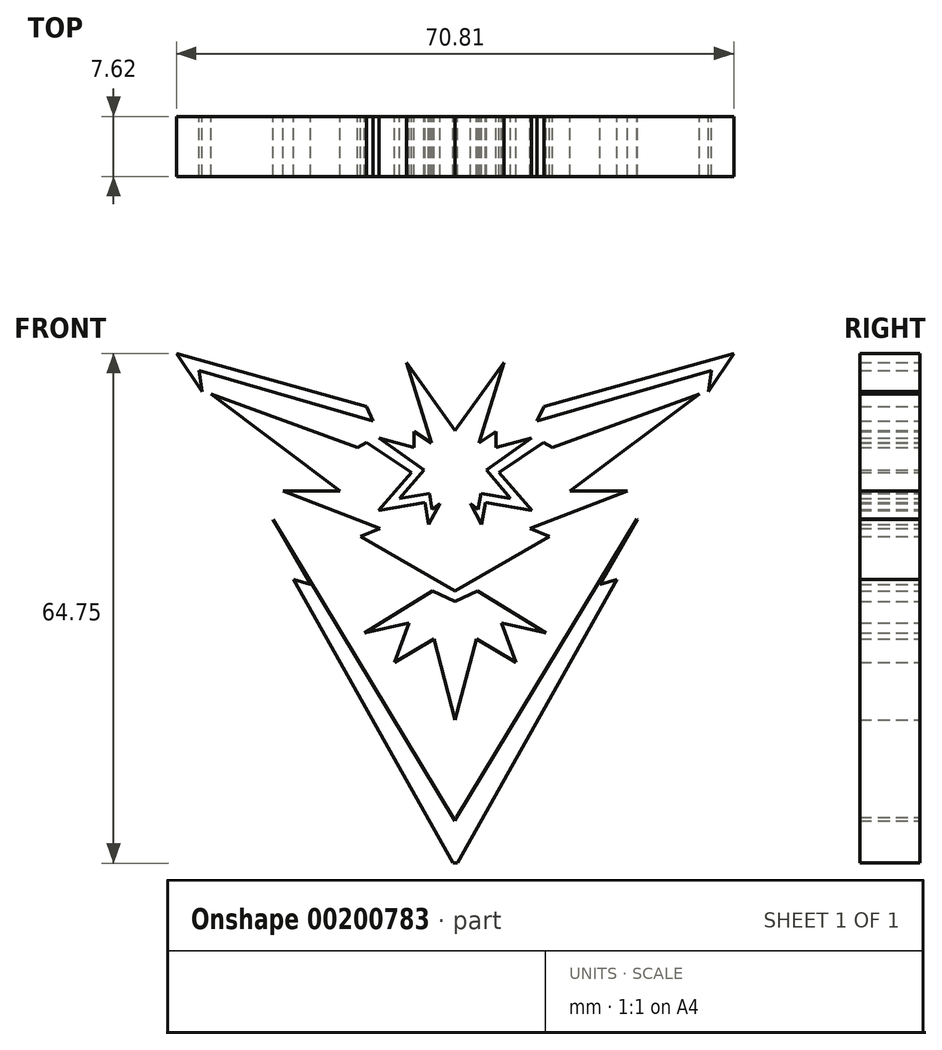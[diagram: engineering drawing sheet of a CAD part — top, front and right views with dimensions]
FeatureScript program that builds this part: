
annotation { "Feature Type Name" : "Feature", "Feature Type Description" : "" }
export const myFeature = defineFeature(function(context is Context, id is Id, definition is map)
    precondition{}
    {
        {
            var Q0;
            Q0=qCreatedBy(makeId("Front.planeOp"),FACE);
            var sketch = newSketch(context, id + "F0", { "sketchPlane" : qUnion([Q0])});
            skLineSegment(sketch, "E0", {"start": v(1.5, 35.4) * mm, "end": v(-4.67, 44.05) * mm});
            skLineSegment(sketch, "E1", {"start": v(-4.67, 44.05) * mm, "end": v(-1.5, 33.83) * mm});
            skLineSegment(sketch, "E2", {"start": v(-1.5, 33.83) * mm, "end": v(-3.69, 35.28) * mm});
            skLineSegment(sketch, "E3", {"start": v(-3.69, 35.28) * mm, "end": v(-3.69, 33.23) * mm});
            skLineSegment(sketch, "E4", {"start": v(-3.69, 33.23) * mm, "end": v(-8.18, 34.47) * mm});
            skLineSegment(sketch, "E5", {"start": v(-8.18, 34.47) * mm, "end": v(-2.45, 30.4) * mm});
            skLineSegment(sketch, "E6", {"start": v(-2.45, 30.4) * mm, "end": v(-5.53, 26.76) * mm});
            skLineSegment(sketch, "E7", {"start": v(-5.53, 26.76) * mm, "end": v(-1.76, 27.4) * mm});
            skLineSegment(sketch, "E8", {"start": v(-1.76, 27.4) * mm, "end": v(-1.42, 25.4) * mm});
            skLineSegment(sketch, "E9", {"start": v(-1.42, 25.4) * mm, "end": v(-0.44, 26.12) * mm});
            skLineSegment(sketch, "E10", {"start": v(-0.44, 26.12) * mm, "end": v(-1.85, 23.47) * mm});
            skLineSegment(sketch, "E11", {"start": v(-1.85, 23.47) * mm, "end": v(-2.32, 26.25) * mm});
            skLineSegment(sketch, "E12", {"start": v(-2.32, 26.25) * mm, "end": v(-8.22, 25.25) * mm});
            skLineSegment(sketch, "E13", {"start": v(-8.22, 25.25) * mm, "end": v(-4.03, 30.06) * mm});
            skLineSegment(sketch, "E14", {"start": v(-4.03, 30.06) * mm, "end": v(-9.72, 33.91) * mm});
            skLineSegment(sketch, "E15", {"start": v(-9.72, 33.91) * mm, "end": v(-10.88, 33.23) * mm});
            skLineSegment(sketch, "E16", {"start": v(-10.88, 33.23) * mm, "end": v(-29.5, 40.03) * mm});
            skLineSegment(sketch, "E17", {"start": v(-29.5, 40.03) * mm, "end": v(-13.1, 27.7) * mm});
            skLineSegment(sketch, "E18", {"start": v(-13.1, 27.7) * mm, "end": v(-20.38, 27.7) * mm});
            skLineSegment(sketch, "E19", {"start": v(-20.38, 27.7) * mm, "end": v(-8.01, 22.95) * mm});
            skLineSegment(sketch, "E20", {"start": v(-8.01, 22.95) * mm, "end": v(-10.5, 21.93) * mm});
            skLineSegment(sketch, "E21", {"start": v(-10.5, 21.93) * mm, "end": v(1.5, 15.01) * mm});
            skLineSegment(sketch, "E22", {"start": v(-1.35, 15.06) * mm, "end": v(-10.01, 9.67) * mm});
            skLineSegment(sketch, "E23", {"start": v(-10.01, 9.67) * mm, "end": v(-4.38, 10.97) * mm});
            skLineSegment(sketch, "E24", {"start": v(-4.38, 10.97) * mm, "end": v(-6.2, 5.95) * mm});
            skLineSegment(sketch, "E25", {"start": v(-6.2, 5.95) * mm, "end": v(-1.17, 8.91) * mm});
            skLineSegment(sketch, "E26", {"start": v(-1.17, 8.91) * mm, "end": v(1.5, -1.33) * mm});
            skLineSegment(sketch, "E27", {"start": v(-1.35, 15.06) * mm, "end": v(1.5, 13.7) * mm});
            skLineSegment(sketch, "E28", {"start": v(-33.9, 45.2) * mm, "end": v(-30.64, 40.35) * mm});
            skLineSegment(sketch, "E29", {"start": v(-30.64, 40.35) * mm, "end": v(-31.05, 43.05) * mm});
            skLineSegment(sketch, "E30", {"start": v(-31.05, 43.05) * mm, "end": v(-8.9, 36.6) * mm});
            skLineSegment(sketch, "E31", {"start": v(-8.9, 36.6) * mm, "end": v(-9.75, 38.47) * mm});
            skLineSegment(sketch, "E32", {"start": v(-9.75, 38.47) * mm, "end": v(-33.9, 45.2) * mm});
            skLineSegment(sketch, "E33", {"start": v(-21.64, 24.13) * mm, "end": v(-16.86, 15.86) * mm});
            skLineSegment(sketch, "E34", {"start": v(-16.86, 15.86) * mm, "end": v(-19.05, 16.5) * mm});
            skLineSegment(sketch, "E35", {"start": v(-19.05, 16.5) * mm, "end": v(1.24, -19.55) * mm});
            skLineSegment(sketch, "E36", {"start": v(-21.64, 24.13) * mm, "end": v(1.24, -13.77) * mm});
            skLineSegment(sketch, "E37.MirrorCS", {"start": v(22.07, 16.5) * mm, "end": v(1.78, -19.55) * mm});
            skLineSegment(sketch, "E38.MirrorCS", {"start": v(24.59, 24.18) * mm, "end": v(1.7, -13.72) * mm});
            skLineSegment(sketch, "E39.MirrorCS", {"start": v(19.88, 15.86) * mm, "end": v(22.07, 16.5) * mm});
            skLineSegment(sketch, "E40.MirrorCS", {"start": v(24.66, 24.13) * mm, "end": v(19.88, 15.86) * mm});
            skLineSegment(sketch, "E41.MirrorCS", {"start": v(4.37, 15.06) * mm, "end": v(13.02, 9.67) * mm});
            skLineSegment(sketch, "E42.MirrorCS", {"start": v(13.02, 9.67) * mm, "end": v(7.4, 10.97) * mm});
            skLineSegment(sketch, "E43.MirrorCS", {"start": v(9.21, 5.95) * mm, "end": v(4.19, 8.91) * mm});
            skLineSegment(sketch, "E44.MirrorCS", {"start": v(7.4, 10.97) * mm, "end": v(9.21, 5.95) * mm});
            skLineSegment(sketch, "E45.MirrorCS", {"start": v(4.19, 8.91) * mm, "end": v(1.5, -1.33) * mm});
            skLineSegment(sketch, "E46.MirrorCS", {"start": v(4.37, 15.06) * mm, "end": v(1.5, 13.7) * mm});
            skLineSegment(sketch, "E47.MirrorCS", {"start": v(13.5, 21.93) * mm, "end": v(1.5, 15.01) * mm});
            skLineSegment(sketch, "E48.MirrorCS", {"start": v(11.03, 22.95) * mm, "end": v(13.5, 21.93) * mm});
            skLineSegment(sketch, "E49.MirrorCS", {"start": v(23.4, 27.7) * mm, "end": v(11.03, 22.95) * mm});
            skLineSegment(sketch, "E50.MirrorCS", {"start": v(16.12, 27.7) * mm, "end": v(23.4, 27.7) * mm});
            skLineSegment(sketch, "E51.MirrorCS", {"start": v(32.51, 40.03) * mm, "end": v(16.12, 27.7) * mm});
            skLineSegment(sketch, "E52.MirrorCS", {"start": v(13.9, 33.23) * mm, "end": v(32.51, 40.03) * mm});
            skLineSegment(sketch, "E53.MirrorCS", {"start": v(12.74, 33.91) * mm, "end": v(13.9, 33.23) * mm});
            skLineSegment(sketch, "E54.MirrorCS", {"start": v(7.05, 30.06) * mm, "end": v(12.74, 33.91) * mm});
            skLineSegment(sketch, "E55.MirrorCS", {"start": v(11.24, 25.25) * mm, "end": v(7.05, 30.06) * mm});
            skLineSegment(sketch, "E56.MirrorCS", {"start": v(5.33, 26.25) * mm, "end": v(11.24, 25.25) * mm});
            skLineSegment(sketch, "E57.MirrorCS", {"start": v(4.86, 23.47) * mm, "end": v(5.33, 26.25) * mm});
            skLineSegment(sketch, "E58.MirrorCS", {"start": v(3.45, 26.12) * mm, "end": v(4.86, 23.47) * mm});
            skLineSegment(sketch, "E59.MirrorCS", {"start": v(4.44, 25.4) * mm, "end": v(3.45, 26.12) * mm});
            skLineSegment(sketch, "E60.MirrorCS", {"start": v(4.78, 27.4) * mm, "end": v(4.44, 25.4) * mm});
            skLineSegment(sketch, "E61.MirrorCS", {"start": v(8.54, 26.76) * mm, "end": v(4.78, 27.4) * mm});
            skLineSegment(sketch, "E62.MirrorCS", {"start": v(5.46, 30.4) * mm, "end": v(8.54, 26.76) * mm});
            skLineSegment(sketch, "E63.MirrorCS", {"start": v(11.2, 34.47) * mm, "end": v(5.46, 30.4) * mm});
            skLineSegment(sketch, "E64.MirrorCS", {"start": v(6.7, 33.23) * mm, "end": v(11.2, 34.47) * mm});
            skLineSegment(sketch, "E65.MirrorCS", {"start": v(6.7, 35.28) * mm, "end": v(6.7, 33.23) * mm});
            skLineSegment(sketch, "E66.MirrorCS", {"start": v(4.52, 33.83) * mm, "end": v(6.7, 35.28) * mm});
            skLineSegment(sketch, "E67.MirrorCS", {"start": v(7.69, 44.05) * mm, "end": v(4.52, 33.83) * mm});
            skLineSegment(sketch, "E68.MirrorCS", {"start": v(1.5, 35.4) * mm, "end": v(7.69, 44.05) * mm});
            skLineSegment(sketch, "E69.MirrorCS", {"start": v(34.06, 43.05) * mm, "end": v(11.91, 36.6) * mm});
            skLineSegment(sketch, "E70.MirrorCS", {"start": v(12.76, 38.47) * mm, "end": v(36.91, 45.2) * mm});
            skLineSegment(sketch, "E71.MirrorCS", {"start": v(11.91, 36.6) * mm, "end": v(12.76, 38.47) * mm});
            skLineSegment(sketch, "E72.MirrorCS", {"start": v(33.65, 40.35) * mm, "end": v(34.06, 43.05) * mm});
            skLineSegment(sketch, "E73.MirrorCS", {"start": v(36.91, 45.2) * mm, "end": v(33.65, 40.35) * mm});
            skLineSegment(sketch, "E74", {"start": v(1.24, -13.77) * mm, "end": v(1.47, -14.16) * mm});
            skLineSegment(sketch, "E75", {"start": v(1.47, -14.16) * mm, "end": v(1.7, -13.72) * mm});
            skLineSegment(sketch, "E76", {"start": v(1.24, -19.55) * mm, "end": v(1.78, -19.55) * mm});
            skLineSegment(sketch, "E77", {"start": v(24.59, 24.18) * mm, "end": v(24.66, 24.13) * mm});
            skSolve(sketch);
        }
        {
            var Q0;
            Q0=makeQuery(id+"F0.imprint","IMPRINT",FACE,{"disambiguationData":[TD([[makeQuery(id+"F0.imprint","IMPRINT",EDGE,{"derivedFrom":sQuery(id+"F0.wireOp",EDGE,"E69.MirrorCS")}),-1.0]])]});
            var Q1;
            Q1=makeQuery(id+"F0.imprint","IMPRINT",FACE,{"disambiguationData":[TD([[makeQuery(id+"F0.imprint","IMPRINT",EDGE,{"derivedFrom":sQuery(id+"F0.wireOp",EDGE,"E33")}),1.0]])]});
            var Q2;
            Q2=makeQuery(id+"F0.imprint","IMPRINT",FACE,{"disambiguationData":[TD([[makeQuery(id+"F0.imprint","IMPRINT",EDGE,{"derivedFrom":sQuery(id+"F0.wireOp",EDGE,"E22")}),1.0]])]});
            var Q3;
            Q3=makeQuery(id+"F0.imprint","IMPRINT",FACE,{"disambiguationData":[TD([[makeQuery(id+"F0.imprint","IMPRINT",EDGE,{"derivedFrom":sQuery(id+"F0.wireOp",EDGE,"E28")}),1.0]])]});
            var Q4;
            Q4=makeQuery(id+"F0.imprint","IMPRINT",FACE,{"disambiguationData":[TD([[makeQuery(id+"F0.imprint","IMPRINT",EDGE,{"derivedFrom":sQuery(id+"F0.wireOp",EDGE,"E0")}),1.0]])]});
            extrude(context, id + "F1", {"entities" : qUnion([Q0, Q1, Q2, Q3, Q4]), "depth" : 7.62 * mm});
        }
    });
